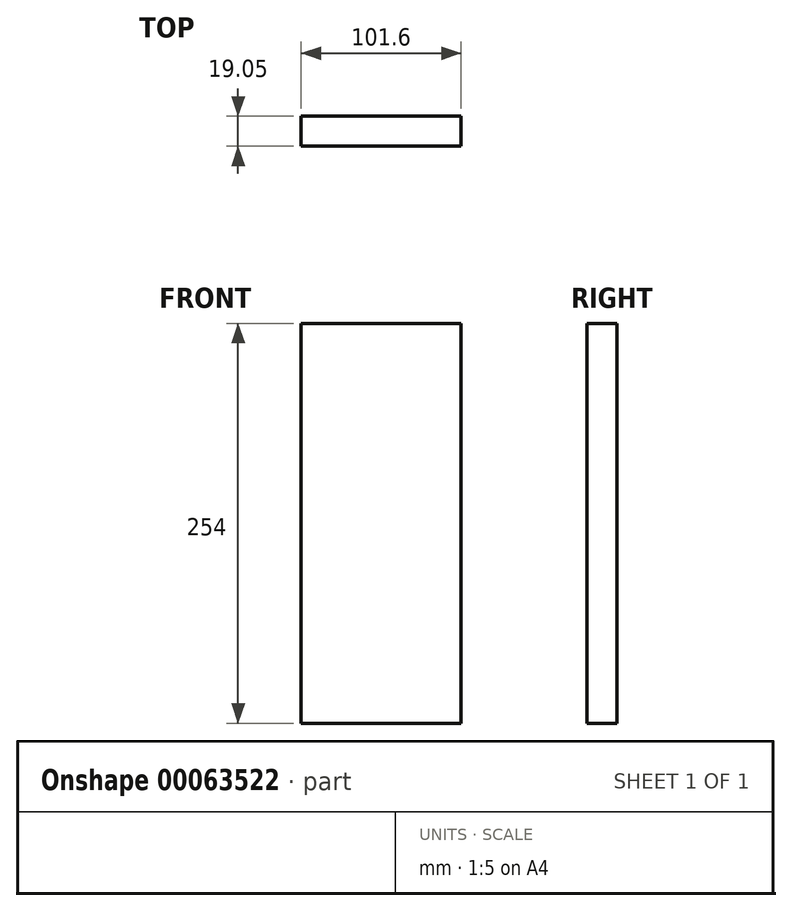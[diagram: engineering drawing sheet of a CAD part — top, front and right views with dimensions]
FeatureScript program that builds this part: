
annotation { "Feature Type Name" : "Feature", "Feature Type Description" : "" }
export const myFeature = defineFeature(function(context is Context, id is Id, definition is map)
    precondition{}
    {
        {
            var Q0;
            Q0=qCreatedBy(makeId("Front.planeOp"),FACE);
            var sketch = newSketch(context, id + "F0", { "sketchPlane" : qUnion([Q0])});
            skLineSegment(sketch, "E0.bottom", {"start": v(-104.79, -104.13) * mm, "end": v(-3.19, -104.13) * mm});
            skLineSegment(sketch, "E0.top", {"start": v(-104.79, -358.13) * mm, "end": v(-3.19, -358.13) * mm});
            skLineSegment(sketch, "E0.left", {"start": v(-104.79, -104.13) * mm, "end": v(-104.79, -358.13) * mm});
            skLineSegment(sketch, "E0.right", {"start": v(-3.19, -104.13) * mm, "end": v(-3.19, -358.13) * mm});
            skSolve(sketch);
        }
        {
            var Q0;
            Q0=makeQuery(id+"F0.imprint","IMPRINT",FACE,{"disambiguationData":[TD([[makeQuery(id+"F0.imprint","IMPRINT",EDGE,{"derivedFrom":sQuery(id+"F0.wireOp",EDGE,"E0.bottom")}),-1.0]])]});
            extrude(context, id + "F1", {"entities" : qUnion([Q0]), "depth" : 19.05 * mm});
        }
    });
